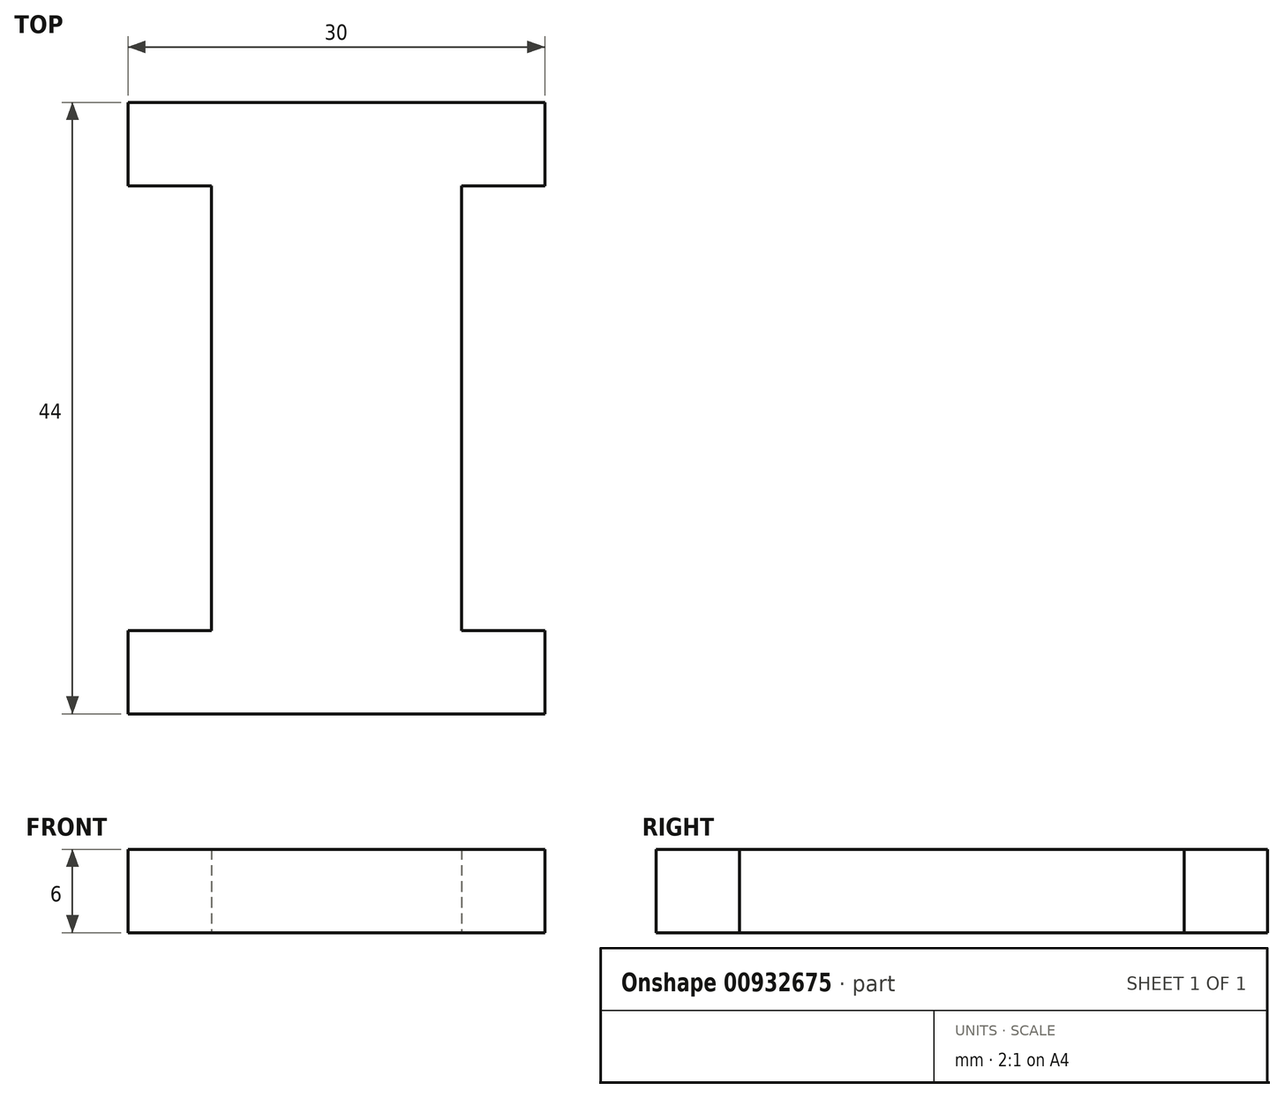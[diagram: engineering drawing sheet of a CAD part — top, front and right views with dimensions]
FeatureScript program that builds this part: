
annotation { "Feature Type Name" : "Feature", "Feature Type Description" : "" }
export const myFeature = defineFeature(function(context is Context, id is Id, definition is map)
    precondition{}
    {
        {
            var Q0;
            Q0=qCreatedBy(makeId("Top.planeOp"),FACE);
            var sketch = newSketch(context, id + "F0", { "sketchPlane" : qUnion([Q0])});
            skLineSegment(sketch, "E0.bottom", {"start": v(15, 22) * mm, "end": v(-15, 22) * mm});
            skLineSegment(sketch, "E0.top", {"start": v(15, -22) * mm, "end": v(-15, -22) * mm});
            skLineSegment(sketch, "E0.left", {"start": v(15, 22) * mm, "end": v(15, 16) * mm});
            skLineSegment(sketch, "E0.right", {"start": v(-15, 22) * mm, "end": v(-15, 16) * mm});
            skPoint(sketch, "E0.middle", {"position": v(0, 0) * mm});
            skLineSegment(sketch, "E1.bottom", {"start": v(15, 16) * mm, "end": v(9, 16) * mm});
            skLineSegment(sketch, "E1.top", {"start": v(15, -16) * mm, "end": v(9, -16) * mm});
            skLineSegment(sketch, "E1.right", {"start": v(9, 16) * mm, "end": v(9, -16) * mm});
            skLineSegment(sketch, "E2.bottom", {"start": v(-15, 16) * mm, "end": v(-9, 16) * mm});
            skLineSegment(sketch, "E2.top", {"start": v(-15, -16) * mm, "end": v(-9, -16) * mm});
            skLineSegment(sketch, "E2.right", {"start": v(-9, 16) * mm, "end": v(-9, -16) * mm});
            skLineSegment(sketch, "E3.trimOffspring", {"start": v(-15, -16) * mm, "end": v(-15, -22) * mm});
            skLineSegment(sketch, "E4.trimOffspring", {"start": v(15, -16) * mm, "end": v(15, -22) * mm});
            skSolve(sketch);
        }
        {
            var Q0;
            Q0=makeQuery(id+"F0.imprint","IMPRINT",FACE,{"disambiguationData":[TD([[makeQuery(id+"F0.imprint","IMPRINT",EDGE,{"derivedFrom":sQuery(id+"F0.wireOp",EDGE,"E0.bottom")}),1.0]])]});
            extrude(context, id + "F1", {"entities" : qUnion([Q0]), "depth" : 6 * mm, "offsetDistance" : 25 * mm});
        }
    });
